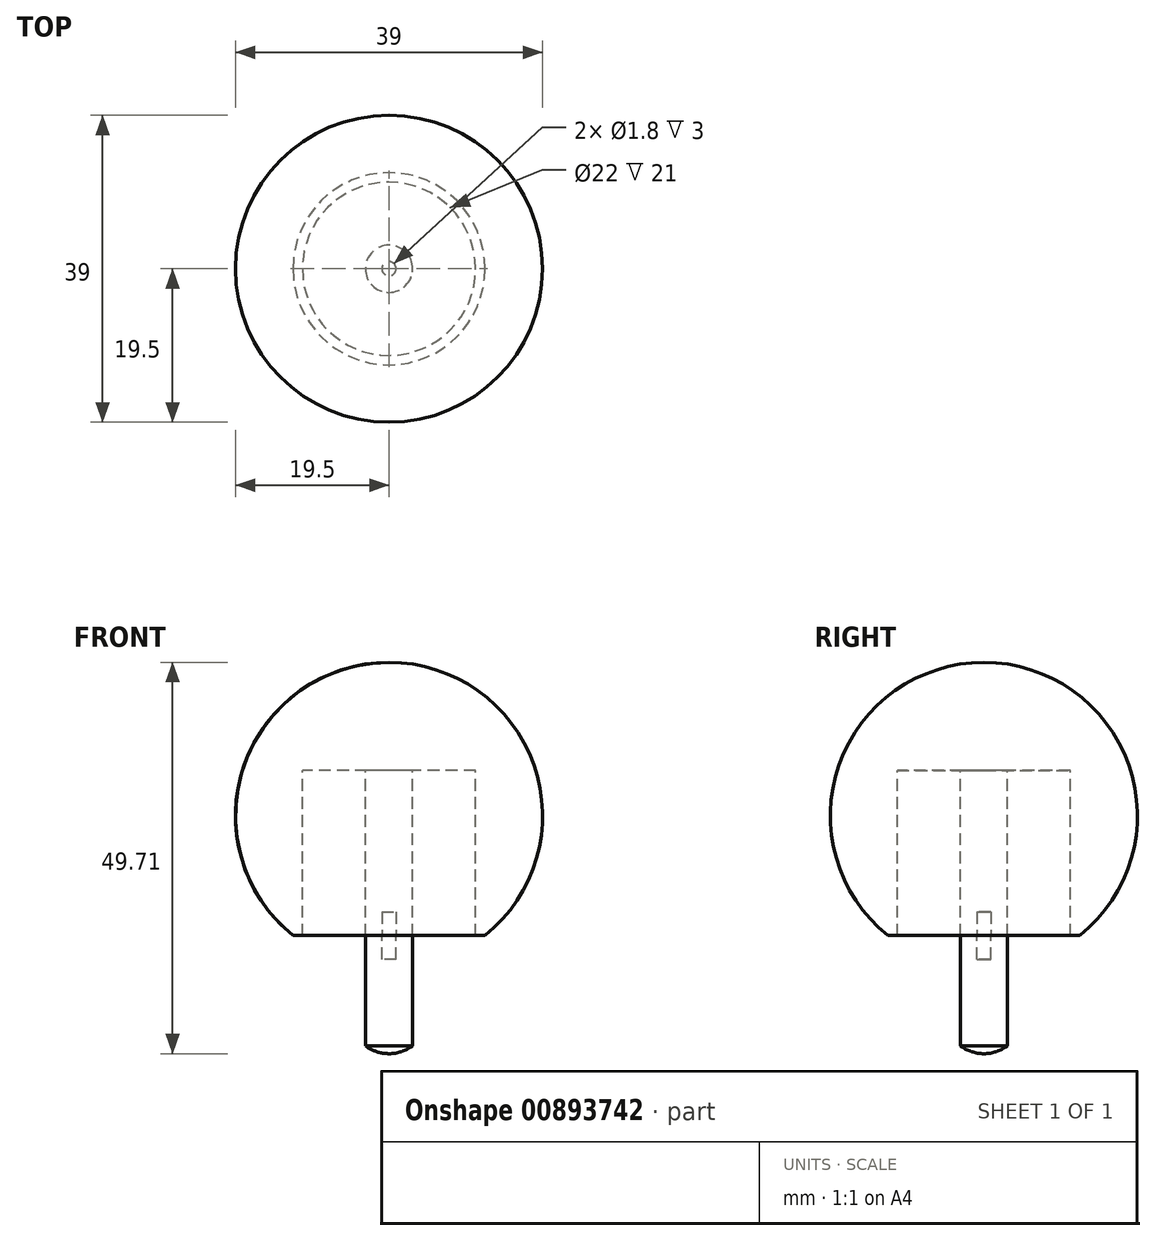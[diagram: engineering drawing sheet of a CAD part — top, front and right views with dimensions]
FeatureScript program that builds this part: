
annotation { "Feature Type Name" : "Feature", "Feature Type Description" : "" }
export const myFeature = defineFeature(function(context is Context, id is Id, definition is map)
    precondition{}
    {
        {
            var Q0;
            Q0=qCreatedBy(makeId("Front.planeOp"),FACE);
            var sketch = newSketch(context, id + "F0", { "sketchPlane" : qUnion([Q0])});
            skArc(sketch, "E0", {"start": v(0, 34.71) * mm, "mid": v(-18.4, 21.68) * mm, "end": v(-12.2, 0) * mm});
            skPoint(sketch, "E1", {"position": v(0, 34.71) * mm});
            skLineSegment(sketch, "E2", {"start": v(-12.2, 0) * mm, "end": v(-11, 0) * mm});
            skLineSegment(sketch, "E3", {"start": v(-3, 21) * mm, "end": v(-3, 0) * mm});
            skLineSegment(sketch, "E4", {"start": v(-3, 0) * mm, "end": v(0, 0) * mm});
            skLineSegment(sketch, "E5", {"start": v(-11, 0) * mm, "end": v(-11, 21) * mm});
            skLineSegment(sketch, "E6", {"start": v(-11, 21) * mm, "end": v(-3, 21) * mm});
            skLineSegment(sketch, "E7", {"start": v(0, 34.71) * mm, "end": v(0, 0) * mm});
            skSolve(sketch);
        }
        {
            var Q0;
            Q0=makeQuery(id+"F0.imprint","IMPRINT",FACE,{"disambiguationData":[TD([[makeQuery(id+"F0.imprint","IMPRINT",EDGE,{"derivedFrom":sQuery(id+"F0.wireOp",EDGE,"E0")}),1.0]])]});
            var Q1;
            Q1=sQuery(id+"F0.wireOp",EDGE,"E7");
            revolve(context, id + "F1", {"surfaceOperationType" : NewSurfaceOperationType.NEW, "entities" : qUnion([Q0]), "axis" : qUnion([Q1]), "revolveType" : RevolveType.FULL});
        }
        {
            var Q0;
            Q0=makeQuery(id+"F1.opRevolve","SWEPT_FACE",FACE,{"disambiguationData":[OSD([sQuery(id+"F0.wireOp",EDGE,"E4")])]});
            extrude(context, id + "F2", {"entities" : qUnion([Q0]), "depth" : 14 * mm, "offsetDistance" : 25 * mm});
        }
        {
            var Q0;
            Q0=qCreatedBy(makeId("Front.planeOp"),FACE);
            var sketch = newSketch(context, id + "F3", { "sketchPlane" : qUnion([Q0])});
            skArc(sketch, "E8", {"start": v(0, -15) * mm, "mid": v(1.58, -14.74) * mm, "end": v(3, -14) * mm});
            skLineSegment(sketch, "E9", {"start": v(3, -14) * mm, "end": v(0, -14) * mm});
            skLineSegment(sketch, "E10", {"start": v(0, -14) * mm, "end": v(0, -15) * mm});
            skLineSegment(sketch, "E11", {"start": v(3, -15) * mm, "end": v(0, -15) * mm, "construction": true});
            skSolve(sketch);
        }
        {
            var Q0;
            Q0=makeQuery(id+"F3.imprint","IMPRINT",FACE,{"disambiguationData":[TD([[makeQuery(id+"F3.imprint","IMPRINT",EDGE,{"derivedFrom":sQuery(id+"F3.wireOp",EDGE,"E8")}),1.0]])]});
            var Q1;
            Q1=sQuery(id+"F3.wireOp",EDGE,"E10");
            revolve(context, id + "F4", {"operationType" : NewBodyOperationType.ADD, "surfaceOperationType" : NewSurfaceOperationType.NEW, "entities" : qUnion([Q0]), "axis" : qUnion([Q1]), "revolveType" : RevolveType.FULL});
        }
        {
            var Q0;
            Q0=makeQuery(id+"F2.opExtrude","CAP_FACE",FACE,{"disambiguationData":[OSD([sQuery(id+"F0.wireOp",EDGE,"E4")])],"isStart":true});
            var sketch = newSketch(context, id + "F5", { "sketchPlane" : qUnion([Q0])});
            skCircle(sketch, "E12", {"center": v(0, 0) * mm, "radius": 0.9 * mm});
            skSolve(sketch);
        }
        {
            var Q0;
            Q0=makeQuery(id+"F5.imprint","IMPRINT",FACE,{"disambiguationData":[TD([[makeQuery(id+"F5.imprint","IMPRINT",EDGE,{"derivedFrom":sQuery(id+"F5.wireOp",EDGE,"E12")}),1.0]])]});
            extrude(context, id + "F6", {"entities" : qUnion([Q0]), "operationType" : NewBodyOperationType.REMOVE, "oppositeDirection" : true, "depth" : 3 * mm, "offsetDistance" : 25 * mm});
        }
        {
            var Q0;
            Q0=makeQuery(id+"F1.opRevolve","SWEPT_FACE",FACE,{"disambiguationData":[OSD([sQuery(id+"F0.wireOp",EDGE,"E4")])]});
            var sketch = newSketch(context, id + "F7", { "sketchPlane" : qUnion([Q0])});
            skCircle(sketch, "E13", {"center": v(0, 0) * mm, "radius": 0.9 * mm});
            skSolve(sketch);
        }
        {
            var Q0;
            Q0=makeQuery(id+"F7.imprint","IMPRINT",FACE,{"disambiguationData":[TD([[makeQuery(id+"F7.imprint","IMPRINT",EDGE,{"derivedFrom":sQuery(id+"F7.wireOp",EDGE,"E13")}),1.0]])]});
            extrude(context, id + "F8", {"entities" : qUnion([Q0]), "operationType" : NewBodyOperationType.REMOVE, "oppositeDirection" : true, "depth" : 3 * mm, "offsetDistance" : 25 * mm});
        }
    });
